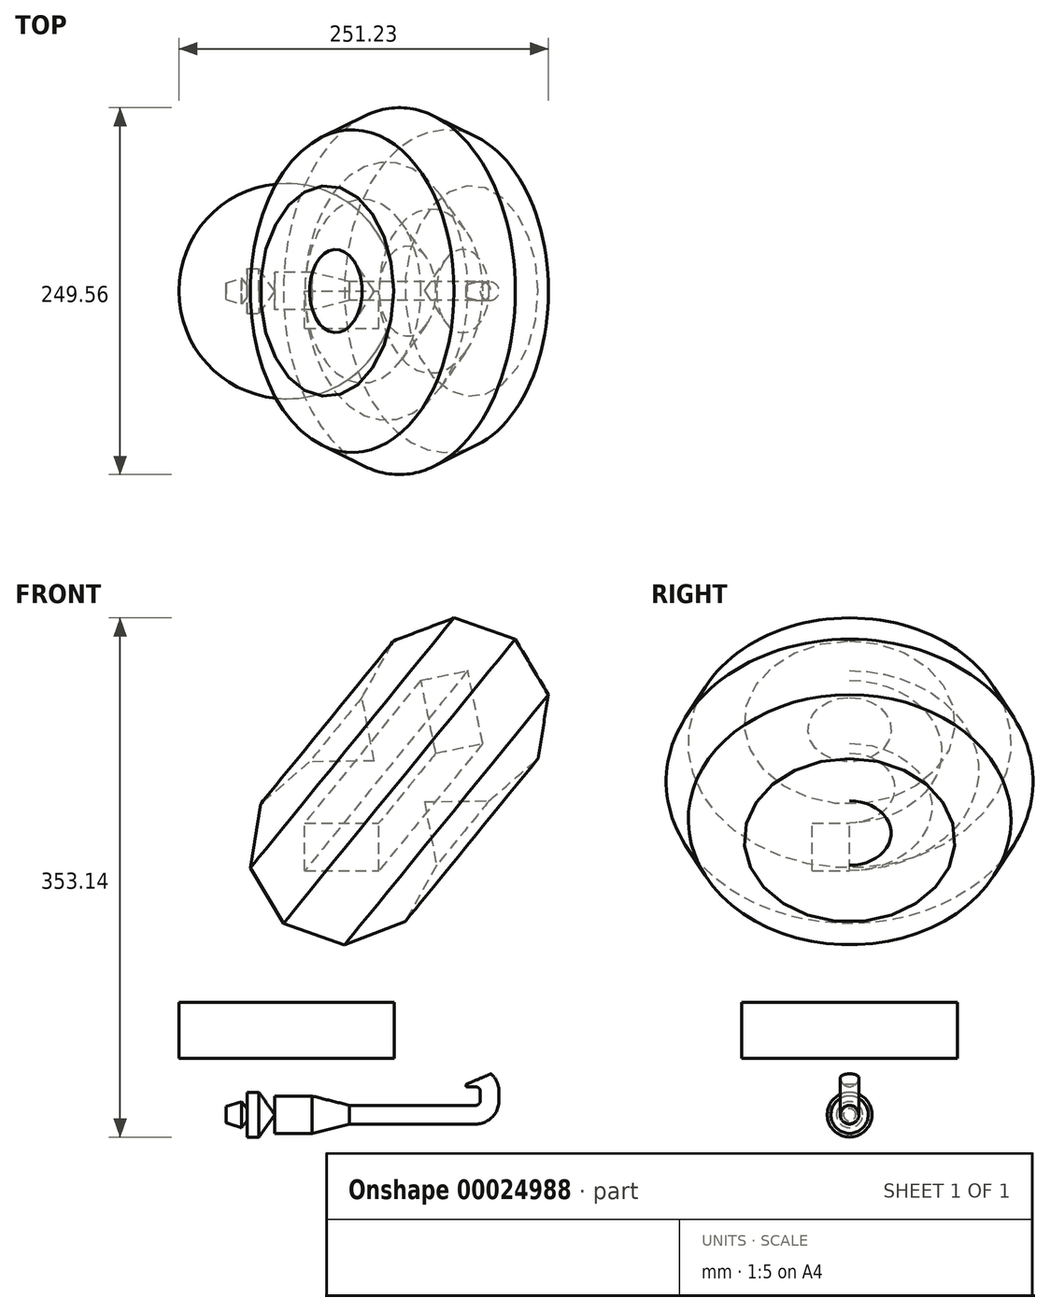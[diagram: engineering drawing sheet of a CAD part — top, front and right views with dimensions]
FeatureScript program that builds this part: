
annotation { "Feature Type Name" : "Feature", "Feature Type Description" : "" }
export const myFeature = defineFeature(function(context is Context, id is Id, definition is map)
    precondition{}
    {
        {
            var Q0;
            Q0=qCreatedBy(makeId("Front.planeOp"),FACE);
            var sketch = newSketch(context, id + "F0", { "sketchPlane" : qUnion([Q0])});
            skLineSegment(sketch, "E0", {"start": v(0, 0) * mm, "end": v(127, 0) * mm});
            skLineSegment(sketch, "E1", {"start": v(127, 0) * mm, "end": v(127, 6.35) * mm});
            skLineSegment(sketch, "E2", {"start": v(127, 6.35) * mm, "end": v(50.8, 6.35) * mm});
            skLineSegment(sketch, "E3", {"start": v(50.8, 6.35) * mm, "end": v(25.4, 12.7) * mm});
            skLineSegment(sketch, "E4", {"start": v(25.4, 12.7) * mm, "end": v(0, 12.7) * mm});
            skLineSegment(sketch, "E5", {"start": v(0, 12.7) * mm, "end": v(0, 0) * mm});
            skSolve(sketch);
        }
        {
            var Q0;
            Q0 = qSketchRegion(id + "F0", true);
            var Q1;
            Q1=sQuery(id+"F0.wireOp",EDGE,"E0");
            revolve(context, id + "F1", {"entities" : qUnion([Q0]), "axis" : qUnion([Q1]), "revolveType" : RevolveType.FULL});
        }
        {
            var Q0;
            Q0=qCreatedBy(makeId("Front.planeOp"),FACE);
            var sketch = newSketch(context, id + "F2", { "sketchPlane" : qUnion([Q0])});
            skLineSegment(sketch, "E6", {"start": v(127, 0) * mm, "end": v(136.53, 0) * mm});
            skLineSegment(sketch, "E7", {"start": v(146.05, 9.53) * mm, "end": v(146.05, 15.88) * mm});
            skLineSegment(sketch, "E8", {"start": v(136.53, 25.4) * mm, "end": v(130.18, 25.4) * mm});
            skPoint(sketch, "E9.visualSharp", {"position": v(146.05, 25.4) * mm});
            skArc(sketch, "E9.filletArc", {"start": v(146.05, 15.88) * mm, "mid": v(143.26, 22.61) * mm, "end": v(136.53, 25.4) * mm});
            skPoint(sketch, "E10.visualSharp", {"position": v(146.05, 0) * mm});
            skArc(sketch, "E10.filletArc", {"start": v(136.53, 0) * mm, "mid": v(143.26, 2.79) * mm, "end": v(146.05, 9.53) * mm});
            skSolve(sketch);
        }
        {
            var Q0;
            Q0=makeQuery(id+"F1.opRevolve","SWEPT_FACE",FACE,{"disambiguationData":[OSD([sQuery(id+"F0.wireOp",EDGE,"E1")])]});
            var sketch = newSketch(context, id + "F3", { "sketchPlane" : qUnion([Q0])});
            skCircle(sketch, "E11", {"center": v(0, 0) * mm, "radius": 6.35 * mm});
            skSolve(sketch);
        }
        {
            var Q0;
            Q0 = qSketchRegion(id + "F3", true);
            var Q1;
            Q1 = qConstructionFilter(qBodyType(qCreatedBy(id + "F2" ,EDGE), BodyType.WIRE), ConstructionObject.NO);
            sweep(context, id + "F4", {"operationType" : NewBodyOperationType.ADD, "profiles" : qUnion([Q0]), "path" : qUnion([Q1])});
        }
        {
            var Q0;
            Q0=qCreatedBy(makeId("Front.planeOp"),FACE);
            var sketch = newSketch(context, id + "F5", { "sketchPlane" : qUnion([Q0])});
            skLineSegment(sketch, "E12", {"start": v(130.18, 20.64) * mm, "end": v(159.73, 33.34) * mm});
            skLineSegment(sketch, "E13", {"start": v(159.73, 33.34) * mm, "end": v(130.18, 33.34) * mm});
            skLineSegment(sketch, "E14", {"start": v(130.18, 33.34) * mm, "end": v(130.18, 20.64) * mm});
            skSolve(sketch);
        }
        {
            var Q0;
            Q0=makeQuery(id+"F5.imprint","IMPRINT",FACE,{"disambiguationData":[TD([[makeQuery(id+"F5.imprint","IMPRINT",EDGE,{"derivedFrom":sQuery(id+"F5.wireOp",EDGE,"E12")}),1.0]])]});
            extrude(context, id + "F6", {"entities" : qUnion([Q0]), "operationType" : NewBodyOperationType.REMOVE, "endBound" : BoundingType.THROUGH_ALL, "oppositeDirection" : true, "depth" : 25.4 * mm, "hasSecondDirection" : true, "secondDirectionBound" : SecondDirectionBoundingType.THROUGH_ALL, "secondDirectionOppositeDirection" : false, "secondDirectionDepth" : 25.4 * mm});
        }
        {
            var Q0;
            Q0=qCreatedBy(makeId("Front.planeOp"),FACE);
            var sketch = newSketch(context, id + "F7", { "sketchPlane" : qUnion([Q0])});
            skLineSegment(sketch, "E15", {"start": v(0, 0) * mm, "end": v(-33.07, 0) * mm});
            skLineSegment(sketch, "E16", {"start": v(-33.07, 0) * mm, "end": v(-33.07, 5.52) * mm});
            skLineSegment(sketch, "E17", {"start": v(-33.07, 5.52) * mm, "end": v(-22.62, 8.85) * mm});
            skLineSegment(sketch, "E18", {"start": v(-22.62, 8.85) * mm, "end": v(-18.9, 4.17) * mm});
            skLineSegment(sketch, "E19", {"start": v(-18.9, 4.17) * mm, "end": v(-18.9, 15.22) * mm});
            skLineSegment(sketch, "E20", {"start": v(-18.9, 15.22) * mm, "end": v(-10.76, 15.22) * mm});
            skLineSegment(sketch, "E21", {"start": v(-10.76, 15.22) * mm, "end": v(0, 0) * mm});
            skSolve(sketch);
        }
        {
            var Q0;
            Q0=makeQuery(id+"F7.imprint","IMPRINT",FACE,{"disambiguationData":[TD([[makeQuery(id+"F7.imprint","IMPRINT",EDGE,{"derivedFrom":sQuery(id+"F7.wireOp",EDGE,"E15")}),-1.0]])]});
            var Q1;
            Q1=sQuery(id+"F7.wireOp",EDGE,"E15");
            revolve(context, id + "F8", {"entities" : qUnion([Q0]), "axis" : qUnion([Q1]), "revolveType" : RevolveType.FULL});
        }
        {
            var Q0;
            Q0=qCreatedBy(makeId("Front.planeOp"),FACE);
            var sketch = newSketch(context, id + "F9", { "sketchPlane" : qUnion([Q0])});
            skLineSegment(sketch, "E22.bottom", {"start": v(8.07, 38.2) * mm, "end": v(81.32, 38.2) * mm});
            skLineSegment(sketch, "E22.top", {"start": v(8.07, 76.3) * mm, "end": v(81.32, 76.3) * mm});
            skLineSegment(sketch, "E22.left", {"start": v(8.07, 38.2) * mm, "end": v(8.07, 76.3) * mm});
            skLineSegment(sketch, "E22.right", {"start": v(81.32, 38.2) * mm, "end": v(81.32, 76.3) * mm});
            skSolve(sketch);
        }
        {
            var Q0;
            Q0=makeQuery(id+"F9.imprint","IMPRINT",FACE,{"disambiguationData":[TD([[makeQuery(id+"F9.imprint","IMPRINT",EDGE,{"derivedFrom":sQuery(id+"F9.wireOp",EDGE,"E22.bottom")}),1.0]])]});
            var Q1;
            Q1=sQuery(id+"F9.wireOp",EDGE,"E22.left");
            revolve(context, id + "F10", {"entities" : qUnion([Q0]), "axis" : qUnion([Q1]), "revolveType" : RevolveType.FULL});
        }
        {
            var Q0;
            Q0=qCreatedBy(makeId("Front.planeOp"),FACE);
            var sketch = newSketch(context, id + "F11", { "sketchPlane" : qUnion([Q0])});
            skLineSegment(sketch, "E23.bottom", {"start": v(20.34, 165.93) * mm, "end": v(70.9, 165.93) * mm});
            skLineSegment(sketch, "E23.top", {"start": v(20.34, 198.47) * mm, "end": v(70.9, 198.47) * mm});
            skLineSegment(sketch, "E23.left", {"start": v(20.34, 165.93) * mm, "end": v(20.34, 198.47) * mm});
            skLineSegment(sketch, "E23.right", {"start": v(70.9, 165.93) * mm, "end": v(70.9, 198.47) * mm});
            skCircle(sketch, "E24.cCircle", {"center": v(46.5, 179.88) * mm, "radius": 60.45 * mm, "construction": true});
            skPoint(sketch, "E24.cCircle.perimeterSnap0", {"position": v(45.62, 198.47) * mm});
            skLineSegment(sketch, "E24.0", {"start": v(23.62, 240) * mm, "end": v(67.62, 240.64) * mm});
            skLineSegment(sketch, "E24.1", {"start": v(67.62, 240.64) * mm, "end": v(101.73, 212.84) * mm});
            skLineSegment(sketch, "E24.2", {"start": v(101.73, 212.84) * mm, "end": v(110, 169.62) * mm});
            skLineSegment(sketch, "E24.3", {"start": v(110, 169.62) * mm, "end": v(88.55, 131.2) * mm});
            skLineSegment(sketch, "E24.4", {"start": v(88.55, 131.2) * mm, "end": v(47.42, 115.55) * mm});
            skLineSegment(sketch, "E24.5", {"start": v(47.42, 115.55) * mm, "end": v(5.86, 130) * mm});
            skLineSegment(sketch, "E24.6", {"start": v(5.86, 130) * mm, "end": v(-16.69, 167.8) * mm});
            skLineSegment(sketch, "E24.7", {"start": v(-16.69, 167.8) * mm, "end": v(-9.67, 211.23) * mm});
            skLineSegment(sketch, "E24.8", {"start": v(-9.67, 211.23) * mm, "end": v(23.62, 240) * mm});
            skPoint(sketch, "E24.0.midPoint", {"position": v(45.62, 240.32) * mm});
            skPoint(sketch, "E24.0.midPoint.positionSnap0", {"position": v(45.62, 198.47) * mm});
            skSolve(sketch);
        }
        {
            var Q0;
            Q0=makeQuery(id+"F11.imprint","IMPRINT",FACE,{"disambiguationData":[TD([[makeQuery(id+"F11.imprint","IMPRINT",EDGE,{"derivedFrom":sQuery(id+"F11.wireOp",EDGE,"E23.bottom")}),1.0]])]});
            extrude(context, id + "F12", {"entities" : qUnion([Q0]), "depth" : 25.4 * mm});
        }
        {
            var Q0;
            Q0 = qSketchRegion(id + "F11", true);
            var Q1;
            Q1=sQuery(id+"F11.wireOp",EDGE,"E24.1");
            revolve(context, id + "F13", {"entities" : qUnion([Q0]), "axis" : qUnion([Q1]), "revolveType" : RevolveType.FULL});
        }
    });
